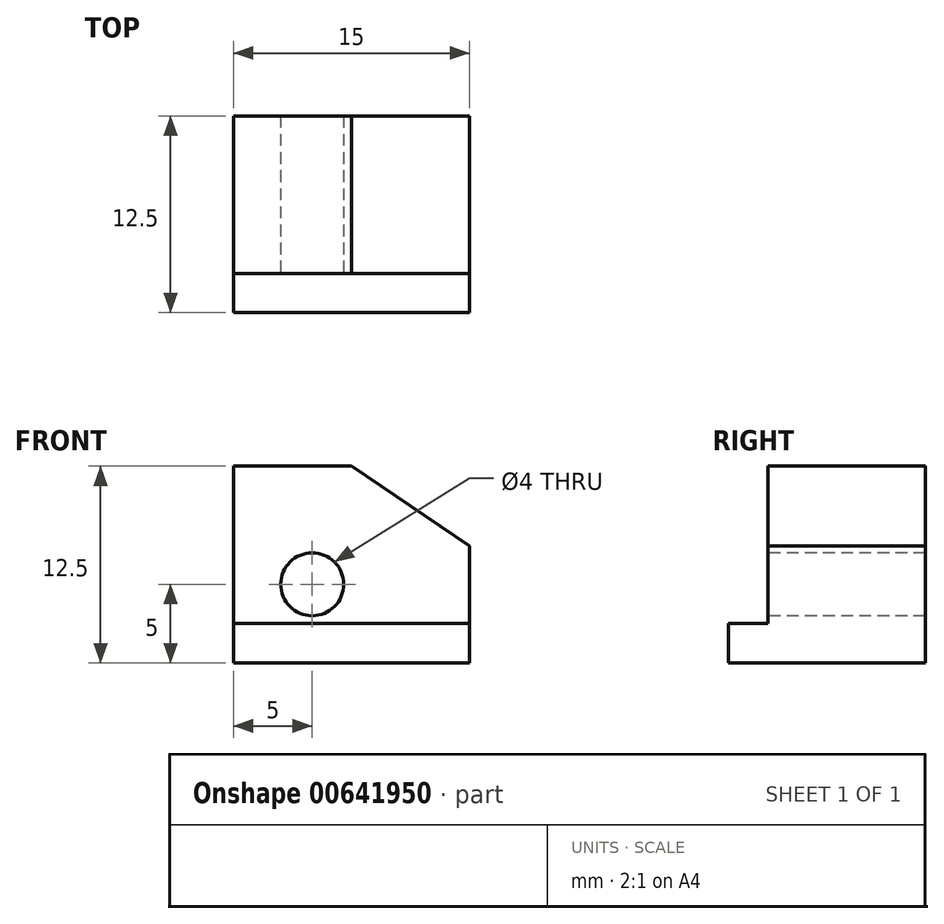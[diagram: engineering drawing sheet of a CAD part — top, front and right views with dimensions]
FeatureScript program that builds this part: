
annotation { "Feature Type Name" : "Feature", "Feature Type Description" : "" }
export const myFeature = defineFeature(function(context is Context, id is Id, definition is map)
    precondition{}
    {
        {
            var Q0;
            Q0=qCreatedBy(makeId("Front.planeOp"),FACE);
            var sketch = newSketch(context, id + "F0", { "sketchPlane" : qUnion([Q0])});
            skLineSegment(sketch, "E0.bottom", {"start": v(-15, 12.5) * mm, "end": v(0, 12.5) * mm});
            skLineSegment(sketch, "E0.top", {"start": v(-15, 0) * mm, "end": v(0, 0) * mm});
            skLineSegment(sketch, "E0.left", {"start": v(-15, 12.5) * mm, "end": v(-15, 0) * mm});
            skLineSegment(sketch, "E0.right", {"start": v(0, 12.5) * mm, "end": v(0, 0) * mm});
            skSolve(sketch);
        }
        {
            var Q0;
            Q0 = qSketchRegion(id + "F0", true);
            extrude(context, id + "F1", {"entities" : qUnion([Q0]), "depth" : 12.5 * mm, "offsetDistance" : 25 * mm});
        }
        {
            var Q0;
            Q0=makeQuery(id+"F1.opExtrude","SWEPT_EDGE",EDGE,{"disambiguationData":[OSD([sQuery(id+"F0.wireOp",EDGE,"E0.bottom"),sQuery(id+"F0.wireOp",EDGE,"E0.right")])]});
            chamfer(context, id + "F2", {"entities" : qUnion([Q0]), "chamferType" : ChamferType.OFFSET_ANGLE, "width" : 7.5 * mm, "oppositeDirection" : false, "angle" : 34 * degree, "tangentPropagation" : true});
        }
        {
            var Q0;
            Q0=makeQuery(id+"F1.opExtrude","SWEPT_FACE",FACE,{"disambiguationData":[OSD([sQuery(id+"F0.wireOp",EDGE,"E0.right")])]});
            var sketch = newSketch(context, id + "F3", { "sketchPlane" : qUnion([Q0])});
            skLineSegment(sketch, "E1.bottom", {"start": v(-12.5, 12.5) * mm, "end": v(-10, 12.5) * mm});
            skLineSegment(sketch, "E1.top", {"start": v(-12.5, 2.5) * mm, "end": v(-10, 2.5) * mm});
            skLineSegment(sketch, "E1.left", {"start": v(-12.5, 12.5) * mm, "end": v(-12.5, 2.5) * mm});
            skLineSegment(sketch, "E1.right", {"start": v(-10, 12.5) * mm, "end": v(-10, 2.5) * mm});
            skSolve(sketch);
        }
        {
            var Q0;
            Q0 = qSketchRegion(id + "F3", true);
            extrude(context, id + "F4", {"entities" : qUnion([Q0]), "operationType" : NewBodyOperationType.REMOVE, "endBound" : BoundingType.THROUGH_ALL, "oppositeDirection" : true, "depth" : 25 * mm, "offsetDistance" : 25 * mm});
        }
        {
            var Q0;
            Q0=makeQuery(id+"F4.boolean.opBoolean","COPY",FACE,{"derivedFrom":makeQuery(id+"F4.opExtrude","SWEPT_FACE",FACE,{"disambiguationData":[OSD([sQuery(id+"F3.wireOp",EDGE,"E1.right")])]})});
            var sketch = newSketch(context, id + "F5", { "sketchPlane" : qUnion([Q0])});
            skCircle(sketch, "E2", {"center": v(-10, 5) * mm, "radius": 2 * mm});
            skSolve(sketch);
        }
        {
            var Q0;
            Q0 = qSketchRegion(id + "F5", true);
            extrude(context, id + "F6", {"entities" : qUnion([Q0]), "operationType" : NewBodyOperationType.REMOVE, "endBound" : BoundingType.THROUGH_ALL, "oppositeDirection" : true, "depth" : 25 * mm, "offsetDistance" : 25 * mm});
        }
    });
